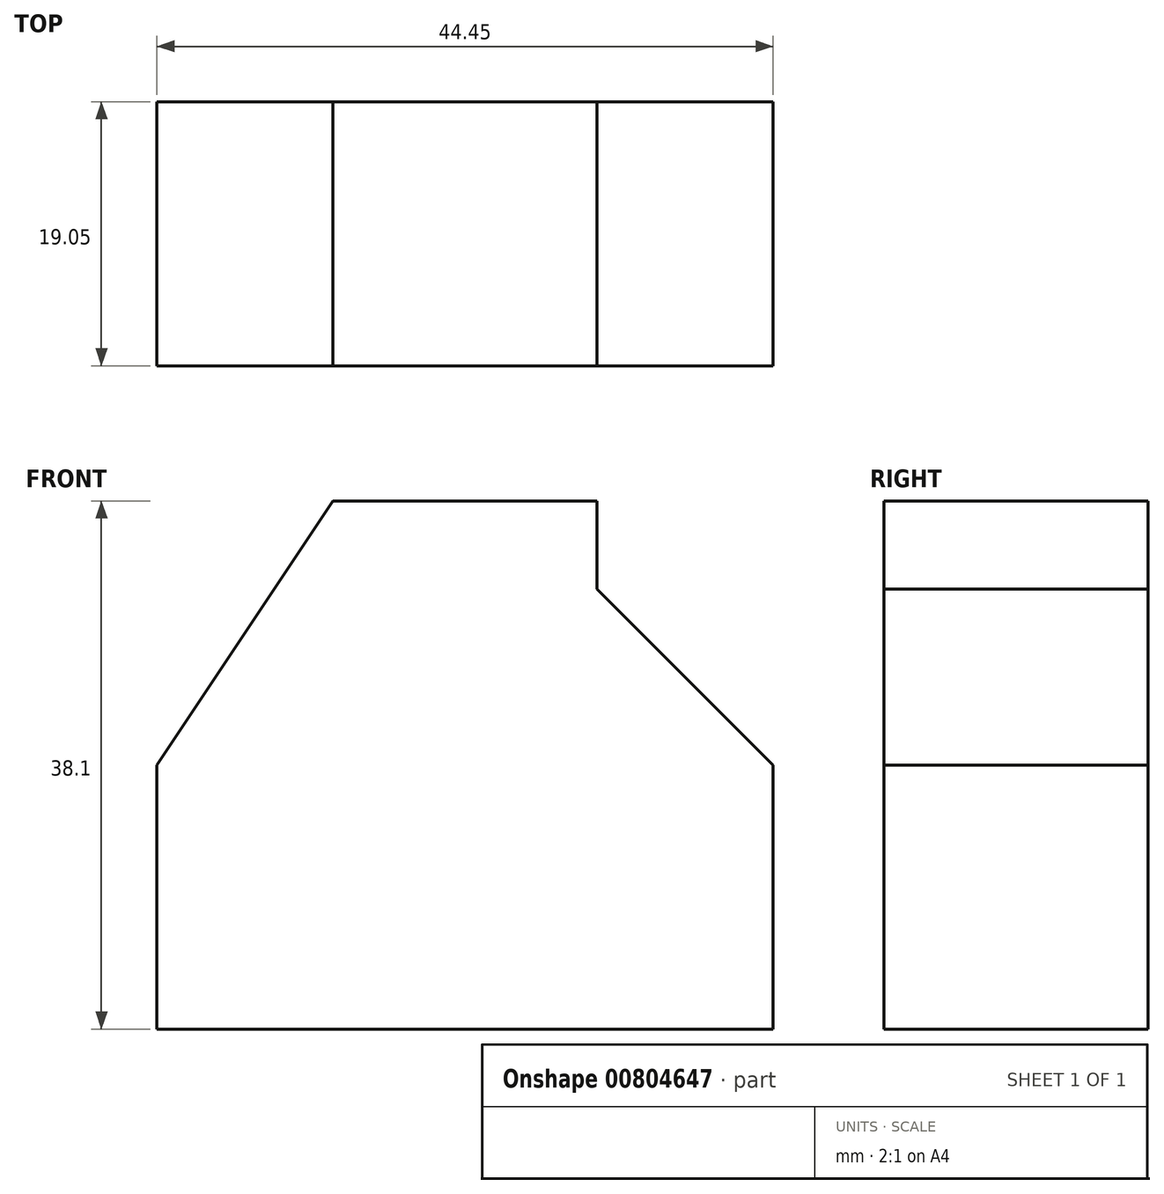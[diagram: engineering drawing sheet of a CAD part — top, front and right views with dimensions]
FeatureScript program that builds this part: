
annotation { "Feature Type Name" : "Feature", "Feature Type Description" : "" }
export const myFeature = defineFeature(function(context is Context, id is Id, definition is map)
    precondition{}
    {
        {
            var Q0;
            Q0=qCreatedBy(makeId("Front.planeOp"),FACE);
            var sketch = newSketch(context, id + "F0", { "sketchPlane" : qUnion([Q0])});
            skLineSegment(sketch, "E0", {"start": v(0, 0) * mm, "end": v(44.45, 0) * mm});
            skLineSegment(sketch, "E1", {"start": v(44.45, 0) * mm, "end": v(44.45, 19.05) * mm});
            skLineSegment(sketch, "E2", {"start": v(0, 0) * mm, "end": v(0, 19.05) * mm});
            skLineSegment(sketch, "E3", {"start": v(0, 0) * mm, "end": v(12.7, 0) * mm, "construction": true});
            skLineSegment(sketch, "E4", {"start": v(12.7, 0) * mm, "end": v(12.7, 38.1) * mm, "construction": true});
            skLineSegment(sketch, "E5", {"start": v(12.7, 38.1) * mm, "end": v(0, 19.05) * mm});
            skLineSegment(sketch, "E6", {"start": v(12.7, 38.1) * mm, "end": v(31.75, 38.1) * mm});
            skLineSegment(sketch, "E7", {"start": v(31.75, 38.1) * mm, "end": v(31.75, 31.75) * mm});
            skLineSegment(sketch, "E8", {"start": v(31.75, 31.75) * mm, "end": v(44.45, 19.05) * mm});
            skSolve(sketch);
        }
        {
            var Q0;
            Q0=makeQuery(id+"F0.imprint","IMPRINT",FACE,{"disambiguationData":[TD([[makeQuery(id+"F0.imprint","IMPRINT",EDGE,{"derivedFrom":sQuery(id+"F0.wireOp",EDGE,"E0")}),1.0]])]});
            extrude(context, id + "F1", {"entities" : qUnion([Q0]), "depth" : 19.05 * mm, "offsetDistance" : 25.4 * mm});
        }
    });
